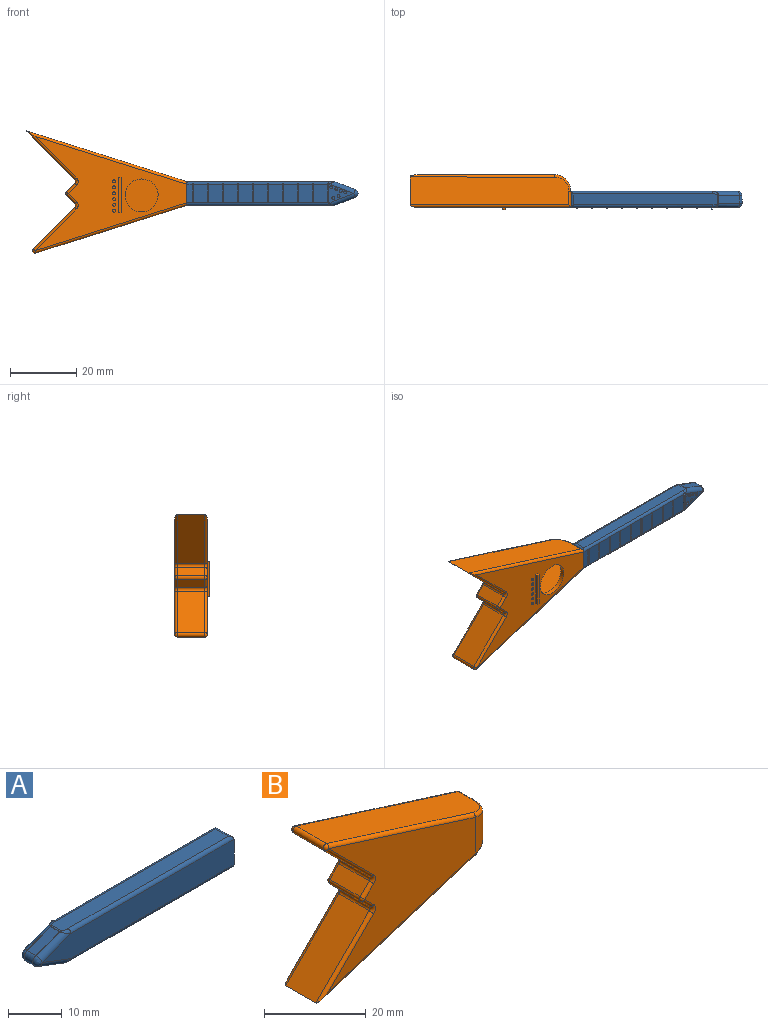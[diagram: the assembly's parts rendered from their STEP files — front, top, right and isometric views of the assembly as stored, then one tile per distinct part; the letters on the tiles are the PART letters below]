
ASSEMBLY  parts=2 mates=1
PART A: 94 faces, bbox 51.6x5.5x8.1 mm
  f0: plane 5.62x0.54mm, normal (1,0,0), area 3mm2, adj f1,f3,f50,f52,f79
  f1: plane 0.54x0.26mm, normal (0,0,1), area 0.1mm2, adj f0,f2,f52,f79
  f2: plane 5.62x0.54mm, normal (-1,0,0), area 3mm2, adj f1,f3,f50,f52,f79
  f3: plane 0.53x0.25mm, normal (0,0,-1), area 0.1mm2, adj f0,f2,f50,f79
  f4: plane 5.62x0.24mm, normal (1,0,0), area 1.3mm2, adj f5,f7,f8,f50,f52
  f5: plane 0.26x0.24mm, normal (0,0,1), area 0.1mm2, adj f4,f6,f8,f52
  f6: plane 5.62x0.24mm, normal (-1,0,0), area 1.3mm2, adj f5,f7,f8,f50,f52
  f7: plane 0.25x0.23mm, normal (0,0,-1), area 0.1mm2, adj f4,f6,f8,f50
  f8: plane 5.61x0.25mm, normal (0,1,0), area 1.4mm2, adj f4,f5,f6,f7
  f9: plane 5.62x0.24mm, normal (1,0,0), area 1.3mm2, adj f10,f12,f13,f50,f52
  f10: plane 0.26x0.24mm, normal (0,0,1), area 0.1mm2, adj f9,f11,f13,f52
  f11: plane 5.62x0.24mm, normal (-1,0,0), area 1.3mm2, adj f10,f12,f13,f50,f52
  f12: plane 0.25x0.23mm, normal (0,0,-1), area 0.1mm2, adj f9,f11,f13,f50
  f13: plane 5.61x0.25mm, normal (0,1,0), area 1.4mm2, adj f9,f10,f11,f12
  f14: plane 5.62x0.24mm, normal (1,0,0), area 1.3mm2, adj f15,f17,f18,f50,f52
  f15: plane 0.26x0.24mm, normal (0,0,1), area 0.1mm2, adj f14,f16,f18,f52
  f16: plane 5.62x0.24mm, normal (-1,0,0), area 1.3mm2, adj f15,f17,f18,f50,f52
  f17: plane 0.25x0.23mm, normal (0,0,-1), area 0.1mm2, adj f14,f16,f18,f50
  f18: plane 5.61x0.25mm, normal (0,1,0), area 1.4mm2, adj f14,f15,f16,f17
  f19: plane 5.62x0.24mm, normal (1,0,0), area 1.3mm2, adj f20,f22,f23,f50,f52
  f20: plane 0.26x0.24mm, normal (0,0,1), area 0.1mm2, adj f19,f21,f23,f52
  f21: plane 5.62x0.24mm, normal (-1,0,0), area 1.3mm2, adj f20,f22,f23,f50,f52
  f22: plane 0.25x0.23mm, normal (0,0,-1), area 0.1mm2, adj f19,f21,f23,f50
  f23: plane 5.61x0.25mm, normal (0,1,0), area 1.4mm2, adj f19,f20,f21,f22
  f24: plane 5.62x0.24mm, normal (1,0,0), area 1.3mm2, adj f25,f27,f28,f50,f52
  f25: plane 0.26x0.24mm, normal (0,0,1), area 0.1mm2, adj f24,f26,f28,f52
  f26: plane 5.62x0.24mm, normal (-1,0,0), area 1.3mm2, adj f25,f27,f28,f50,f52
  f27: plane 0.25x0.23mm, normal (0,0,-1), area 0.1mm2, adj f24,f26,f28,f50
  f28: plane 5.61x0.25mm, normal (0,1,0), area 1.4mm2, adj f24,f25,f26,f27
  f29: plane 5.62x0.24mm, normal (1,0,0), area 1.3mm2, adj f30,f32,f33,f50,f52
  f30: plane 0.26x0.24mm, normal (0,0,1), area 0.1mm2, adj f29,f31,f33,f52
  f31: plane 5.62x0.24mm, normal (-1,0,0), area 1.3mm2, adj f30,f32,f33,f50,f52
  f32: plane 0.25x0.23mm, normal (0,0,-1), area 0.1mm2, adj f29,f31,f33,f50
  f33: plane 5.61x0.25mm, normal (0,1,0), area 1.4mm2, adj f29,f30,f31,f32
  f34: plane 5.62x0.24mm, normal (1,0,0), area 1.3mm2, adj f35,f37,f38,f50,f52
  f35: plane 0.26x0.24mm, normal (0,0,1), area 0.1mm2, adj f34,f36,f38,f52
  f36: plane 5.62x0.24mm, normal (-1,0,0), area 1.3mm2, adj f35,f37,f38,f50,f52
  f37: plane 0.25x0.23mm, normal (0,0,-1), area 0.1mm2, adj f34,f36,f38,f50
  f38: plane 5.61x0.25mm, normal (0,1,0), area 1.4mm2, adj f34,f35,f36,f37
  f39: plane 5.62x0.24mm, normal (1,0,0), area 1.3mm2, adj f40,f42,f43,f50,f52
  f40: plane 0.26x0.24mm, normal (0,0,1), area 0.1mm2, adj f39,f41,f43,f52
  f41: plane 5.62x0.24mm, normal (-1,0,0), area 1.3mm2, adj f40,f42,f43,f50,f52
  f42: plane 0.25x0.23mm, normal (0,0,-1), area 0.1mm2, adj f39,f41,f43,f50
  f43: plane 5.61x0.25mm, normal (0,1,0), area 1.4mm2, adj f39,f40,f41,f42
  f44: plane 5.69x4.83mm, normal (1,0,0), area 27.5mm2, adj f49,f50,f53,f56
  f45: plane 43.46x3.3mm, normal (0,0,1), area 143.2mm2, adj f51,f52,f53,f57,f60,f65
  f46: plane 6.15x2.34mm, normal (-0.35,0,0.93), area 15mm2, adj f59,f60,f67,f68
  f47: plane 6.15x2.34mm, normal (-0.35,0,-0.93), area 15mm2, adj f62,f67,f69,f72
  f48: plane 43.46x3.3mm, normal (0,0,-1), area 143.2mm2, adj f54,f55,f56,f61,f69,f73
  f49: plane 50.37x5.69mm, normal (0,-1,0), area 265.3mm2, adj f44,f51,f54,f68,f72
  f50: plane 50.37x5.69mm, normal (0,1,0), area 247.5mm2, adj f0,f2,f3,f4,f6,f7,f9,f11
  f51: cylinder r=0.76mm len=42.88mm, axis (1,0,0), area 50.9mm2, adj f45,f49,f53,f65
  f52: cylinder r=0.76mm len=42.88mm, axis (-1,0,0), area 50.8mm2, adj f0,f1,f2,f4,f5,f6,f9,f10
  f53: cylinder r=0.76mm len=4.83mm, axis (0,-1,0), area 4.9mm2, adj f44,f45,f51,f52
  f54: cylinder r=0.76mm len=42.88mm, axis (-1,0,0), area 50.9mm2, adj f48,f49,f56,f73
  f55: cylinder r=0.76mm len=42.88mm, axis (1,0,0), area 50.9mm2, adj f48,f50,f56,f61
  f56: cylinder r=0.76mm len=4.83mm, axis (0,1,0), area 4.9mm2, adj f44,f48,f54,f55
  f57: bspline ~1.97x1.28mm, area 1.3mm2, adj f45,f52,f58,f59
  f58: bspline ~0.53x0.52mm, area 0.1mm2, adj f57,f59,f60
  f59: cylinder r=1.27mm len=7.94mm, axis (-0.93,0,-0.35), area 14.4mm2, adj f46,f50,f57,f58,f63
  f60: cylinder r=1.27mm len=2.65mm, axis (0,1,0), area 1.1mm2, adj f45,f46,f58,f64
  f61: bspline ~1.97x1.28mm, area 1.3mm2, adj f48,f55,f62,f66
  f62: cylinder r=1.27mm len=7.94mm, axis (0.93,0,-0.35), area 14.4mm2, adj f47,f50,f61,f63,f66
  f63: sphere r=1.27mm, area 2.7mm2, adj f59,f62,f67
  f64: bspline ~0.53x0.52mm, area 0.1mm2, adj f60,f65,f68
  f65: bspline ~1.97x1.28mm, area 1.3mm2, adj f45,f51,f64,f68
  f66: bspline ~0.53x0.52mm, area 0.1mm2, adj f61,f62,f69
  f67: cylinder r=1.27mm len=2.37mm, axis (0,-1,0), area 7mm2, adj f46,f47,f63,f70
  f68: cylinder r=1.27mm len=7.94mm, axis (0.93,0,0.35), area 14.4mm2, adj f46,f49,f64,f65,f70
  f69: cylinder r=1.27mm len=2.65mm, axis (0,1,0), area 1.1mm2, adj f47,f48,f66,f71
  f70: sphere r=1.27mm, area 2.7mm2, adj f67,f68,f72
  f71: bspline ~0.53x0.52mm, area 0.1mm2, adj f69,f72,f73
  f72: cylinder r=1.27mm len=7.94mm, axis (-0.93,0,0.35), area 14.4mm2, adj f47,f49,f70,f71,f73
  f73: bspline ~1.97x1.28mm, area 1.3mm2, adj f48,f54,f71,f72
  f74: plane 5.62x0.24mm, normal (1,0,0), area 1.3mm2, adj f50,f52,f75,f77,f78
  f75: plane 0.26x0.24mm, normal (0,0,1), area 0.1mm2, adj f52,f74,f76,f78
  f76: plane 5.62x0.24mm, normal (-1,0,0), area 1.3mm2, adj f50,f52,f75,f77,f78
  f77: plane 0.25x0.23mm, normal (0,0,-1), area 0.1mm2, adj f50,f74,f76,f78
  f78: plane 5.61x0.25mm, normal (0,1,0), area 1.4mm2, adj f74,f75,f76,f77
  f79: plane 5.61x0.25mm, normal (0,1,0), area 1.4mm2, adj f0,f1,f2,f3
  f80: cylinder r=0.44mm len=0.89mm, axis (0,1,0), area 2.1mm2, adj f50,f81
  f81: plane 0.89x0.89mm, normal (0,1,0), area 0.6mm2, adj f80
  f82: cylinder r=0.04mm len=0.74mm, axis (0,1,0), area 0.2mm2, adj f84,f85
  f83: cylinder r=0.44mm len=0.89mm, axis (0,1,0), area 2.1mm2, adj f50,f84
  f84: plane 0.89x0.89mm, normal (0,1,0), area 0.6mm2, adj f82,f83
  f85: plane 0.09x0.09mm, normal (0,1,0), area 0mm2, adj f82
  f86: cylinder r=0.44mm len=0.89mm, axis (0,1,0), area 2.1mm2, adj f50,f87
  f87: plane 0.89x0.89mm, normal (0,1,0), area 0.6mm2, adj f86
  f88: cylinder r=0.44mm len=0.89mm, axis (0,1,0), area 2.1mm2, adj f50,f89
  f89: plane 0.89x0.89mm, normal (0,1,0), area 0.6mm2, adj f88
  f90: cylinder r=0.44mm len=0.89mm, axis (0,1,0), area 2.1mm2, adj f50,f91
  f91: plane 0.89x0.89mm, normal (0,1,0), area 0.6mm2, adj f90
  f92: cylinder r=0.44mm len=0.89mm, axis (0,1,0), area 2.1mm2, adj f50,f93
  f93: plane 0.89x0.89mm, normal (0,1,0), area 0.6mm2, adj f92
PART B: 72 faces, bbox 49.4x11.1x37.9 mm
  f0: plane 45.71x34.41mm, normal (0,1,0), area 555.3mm2, adj f1,f20,f21,f22,f23,f24,f26,f28
  f1: plane 6.07x0.51mm, normal (1,0,0), area 3.1mm2, adj f0,f59,f65,f69,f70,f71
  f2: plane 44.95x14.17mm, normal (0.3,0,0.95), area 390.8mm2, adj f48,f52,f58,f59,f65
  f3: plane 12.54x12.54mm, normal (-0.71,0,-0.71), area 148.6mm2, adj f40,f42,f48,f49
  f4: plane 8.38x2.51mm, normal (-0.71,0,0.71), area 29.8mm2, adj f38,f40,f44,f45
  f5: plane 8.38x2.51mm, normal (-0.71,0,-0.71), area 29.8mm2, adj f45,f46,f54,f55
  f6: plane 14.74x14.74mm, normal (-0.71,0,0.71), area 174.7mm2, adj f7,f55,f57,f66
  f7: plane 47.92x15.11mm, normal (0.3,0,-0.95), area 416.9mm2, adj f6,f61,f67,f70,f71
  f8: plane 40.63x34.41mm, normal (0,-1,0), area 608.4mm2, adj f9,f38,f39,f42,f46,f51,f52,f57
  f9: cylinder r=5.08mm len=8.79mm, axis (0,0,-1), area 52.7mm2, adj f8,f58,f62,f67
  f10: plane 5.32x0.44mm, normal (0,1,0), area 2.3mm2, adj f11,f16,f19,f62,f64,f68
  f11: plane 43.39x14.03mm, normal (-0.3,0,-0.95), area 326.9mm2, adj f10,f12,f17,f18,f19,f64
  f12: plane 12.51x12.51mm, normal (0.71,0,0.71), area 130.3mm2, adj f11,f13,f17,f18
  f13: plane 7.37x3.59mm, normal (0.71,0,-0.71), area 37.4mm2, adj f12,f14,f17,f18
  f14: plane 7.37x3.59mm, normal (0.71,0,0.71), area 37.4mm2, adj f13,f15,f17,f18
  f15: plane 12.51x12.51mm, normal (0.71,0,-0.71), area 130.3mm2, adj f14,f16,f17,f18
  f16: plane 43.39x14.03mm, normal (-0.3,0,0.95), area 326.9mm2, adj f10,f15,f17,f18,f19,f68
  f17: plane 38.8x32.2mm, normal (0,1,0), area 541.1mm2, adj f11,f12,f13,f14,f15,f16,f19
  f18: plane 43.12x32.2mm, normal (0,-1,0), area 490.7mm2, adj f11,f12,f13,f14,f15,f16,f20,f64
  f19: cylinder r=3.81mm len=7.72mm, axis (0,0,-1), area 39mm2, adj f10,f11,f16,f17
  f20: cylinder r=4.98mm len=9.96mm, axis (0,1,0), area 39.7mm2, adj f0,f18
  f21: plane 10.67x0.64mm, normal (1,0,0), area 6.8mm2, adj f0,f22,f24,f25
  f22: plane 0.76x0.64mm, normal (0,0,1), area 0.5mm2, adj f0,f21,f23,f25
  f23: plane 10.67x0.64mm, normal (-1,0,0), area 6.8mm2, adj f0,f22,f24,f25
  f24: plane 0.76x0.64mm, normal (0,0,-1), area 0.5mm2, adj f0,f21,f23,f25
  f25: plane 10.67x0.76mm, normal (0,1,0), area 8.1mm2, adj f21,f22,f23,f24
  f26: cylinder r=0.44mm len=0.87mm, axis (0,1,0), area 1.2mm2, adj f0,f27
  f27: plane 0.87x0.87mm, normal (0,1,0), area 0.6mm2, adj f26
  f28: cylinder r=0.44mm len=0.87mm, axis (0,1,0), area 1.2mm2, adj f0,f29
  f29: plane 0.87x0.87mm, normal (0,1,0), area 0.6mm2, adj f28
  f30: cylinder r=0.44mm len=0.87mm, axis (0,1,0), area 1.2mm2, adj f0,f31
  f31: plane 0.87x0.87mm, normal (0,1,0), area 0.6mm2, adj f30
  f32: cylinder r=0.44mm len=0.87mm, axis (0,1,0), area 1.2mm2, adj f0,f33
  f33: plane 0.87x0.87mm, normal (0,1,0), area 0.6mm2, adj f32
  f34: cylinder r=0.44mm len=0.87mm, axis (0,1,0), area 1.2mm2, adj f0,f35
  f35: plane 0.87x0.87mm, normal (0,1,0), area 0.6mm2, adj f34
  f36: cylinder r=0.44mm len=0.87mm, axis (0,1,0), area 1.2mm2, adj f0,f37
  f37: plane 0.87x0.87mm, normal (0,1,0), area 0.6mm2, adj f36
  f38: cylinder r=0.76mm len=3.05mm, axis (0.71,0,0.71), area 4.3mm2, adj f4,f8,f39,f41
  f39: torus R=1.52mm, axis (0,-1,0), area 2mm2, adj f8,f38,f40,f42
  f40: cylinder r=0.76mm len=8.38mm, axis (0,-1,0), area 10mm2, adj f3,f4,f39,f43
  f41: sphere r=0.76mm, area 0.7mm2, adj f38,f45,f46
  f42: cylinder r=0.76mm len=13.08mm, axis (-0.71,0,0.71), area 21.2mm2, adj f3,f8,f39,f47
  f43: torus R=1.52mm, axis (0,-1,0), area 2mm2, adj f0,f40,f44,f49
  f44: cylinder r=0.76mm len=3.05mm, axis (-0.71,0,-0.71), area 4.3mm2, adj f0,f4,f43,f50
  f45: cylinder r=0.76mm len=8.38mm, axis (0,1,0), area 10mm2, adj f4,f5,f41,f50
  f46: cylinder r=0.76mm len=3.05mm, axis (-0.71,0,0.71), area 4.3mm2, adj f5,f8,f41,f51
  f47: sphere r=0.76mm, area 1.5mm2, adj f42,f48,f52
  f48: cylinder r=0.76mm len=8.38mm, axis (0,-1,0), area 17mm2, adj f2,f3,f47,f53
  f49: cylinder r=0.76mm len=13.08mm, axis (0.71,0,-0.71), area 21.2mm2, adj f0,f3,f43,f53
  f50: sphere r=0.76mm, area 0.7mm2, adj f44,f45,f54
  f51: torus R=1.52mm, axis (0,-1,0), area 2mm2, adj f8,f46,f55,f57
  f52: cylinder r=0.76mm len=40.86mm, axis (0.95,0,-0.3), area 51mm2, adj f2,f8,f47,f58
  f53: sphere r=0.76mm, area 1.5mm2, adj f48,f49,f59
  f54: cylinder r=0.76mm len=3.05mm, axis (0.71,0,-0.71), area 4.3mm2, adj f0,f5,f50,f60
  f55: cylinder r=0.76mm len=8.38mm, axis (0,-1,0), area 10mm2, adj f5,f6,f51,f60
  f56: bspline ~1.62x1.19mm, area 0.4mm2, adj f58,f62,f64
  f57: cylinder r=0.76mm len=15.28mm, axis (0.71,0,0.71), area 23.6mm2, adj f6,f8,f51,f61
  f58: bspline ~5.96x5.09mm, area 7.9mm2, adj f2,f9,f52,f56,f62,f65
  f59: cylinder r=0.76mm len=45.94mm, axis (-0.95,0,0.3), area 56.9mm2, adj f0,f1,f2,f53,f65
  f60: torus R=1.52mm, axis (0,-1,0), area 2mm2, adj f0,f54,f55,f66
  f61: cylinder r=0.76mm len=43.83mm, axis (-0.95,0,-0.3), area 53.4mm2, adj f7,f8,f57,f67
  f62: cylinder r=0.76mm len=6.36mm, axis (0,0,-1), area 7.4mm2, adj f9,f10,f56,f58,f63,f67
  f63: bspline ~1.86x1.19mm, area 0.4mm2, adj f62,f67,f68
  f64: cylinder r=0.76mm len=4.19mm, axis (0,-1,0), area 4.8mm2, adj f10,f11,f18,f56,f65,f69
  f65: cylinder r=0.76mm len=4.79mm, axis (0,1,0), area 3.7mm2, adj f1,f2,f58,f59,f64,f69
  f66: cylinder r=0.76mm len=15.28mm, axis (-0.71,0,-0.71), area 23.6mm2, adj f0,f6,f60,f70
  f67: bspline ~5.31x5.3mm, area 7.9mm2, adj f7,f9,f61,f62,f63,f71
  f68: cylinder r=0.76mm len=4.19mm, axis (0,1,0), area 4.8mm2, adj f10,f16,f18,f63,f69,f71
  f69: cylinder r=0.76mm len=6.33mm, axis (0,0,-1), area 6.7mm2, adj f1,f18,f64,f65,f68,f71
  f70: cylinder r=0.76mm len=48.91mm, axis (0.95,0,0.3), area 59.3mm2, adj f0,f1,f7,f66,f71
  f71: cylinder r=0.76mm len=4.79mm, axis (0,-1,0), area 3.7mm2, adj f1,f7,f67,f68,f69,f70
PLACE A rot(axis=(0,0,-1),180deg) t=(71.86,-68.39,25.7)mm
PLACE B rot(axis=(-1,0,0),180deg) t=(79.7,-68.39,70.12)mm
MATE fastened A.f44 <-> B.f1  axis (-1,0,0) through (59.71,-68.39,42.05)mm
